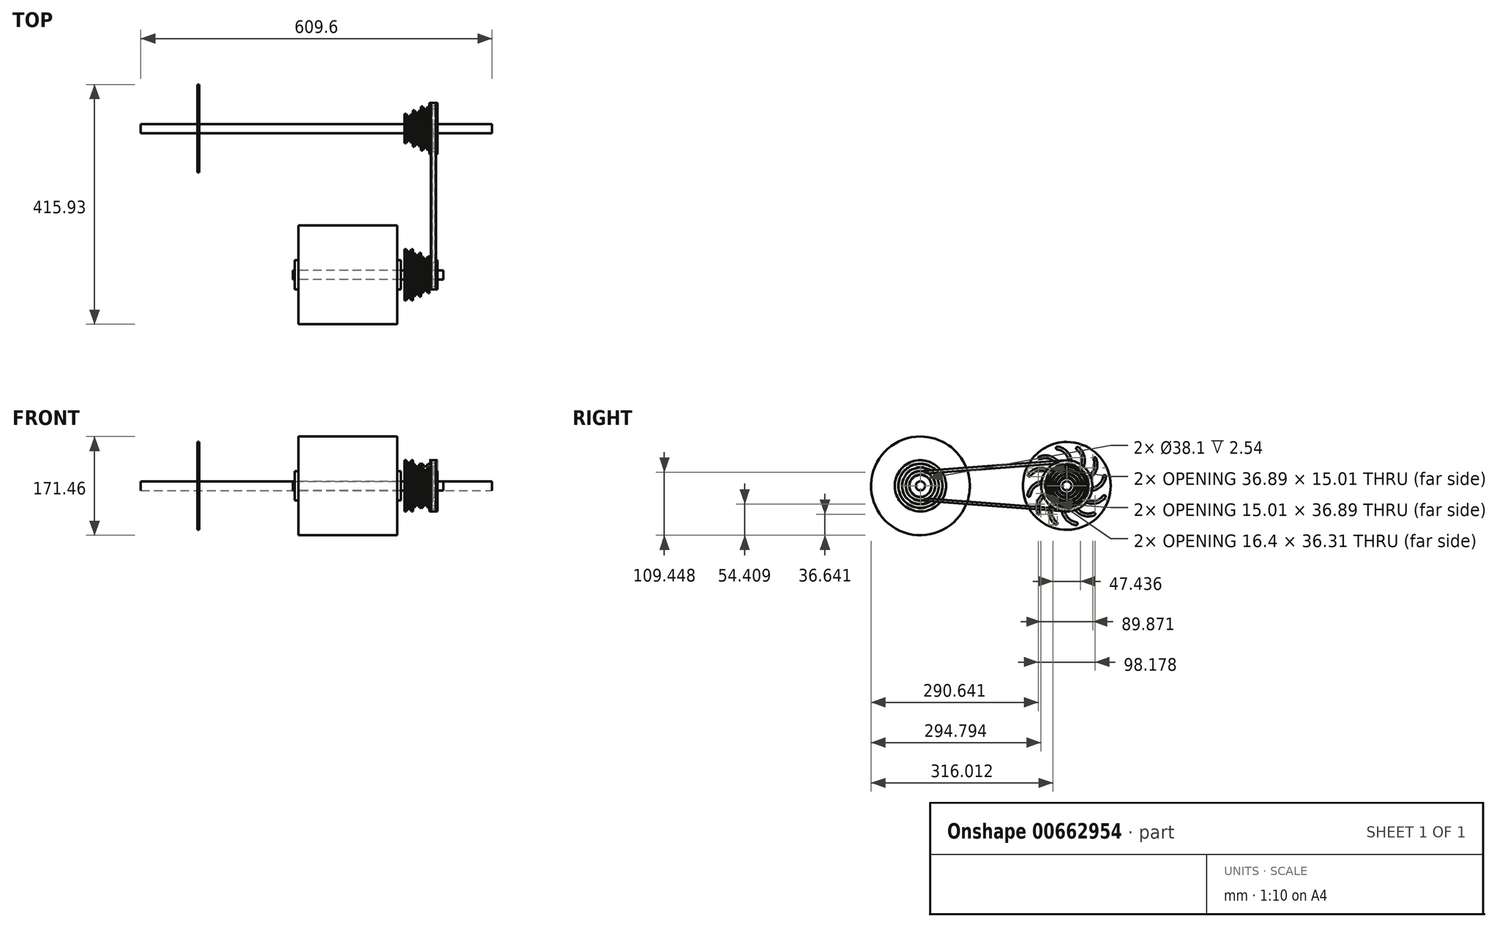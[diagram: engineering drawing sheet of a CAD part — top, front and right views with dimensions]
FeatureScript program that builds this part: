
annotation { "Feature Type Name" : "Feature", "Feature Type Description" : "" }
export const myFeature = defineFeature(function(context is Context, id is Id, definition is map)
    precondition{}
    {
        {
            var Q0;
            Q0=qCreatedBy(makeId("Right.planeOp"),FACE);
            var sketch = newSketch(context, id + "F0", { "sketchPlane" : qUnion([Q0])});
            skCircle(sketch, "E0", {"center": v(0, 0) * mm, "radius": 85.72 * mm});
            skCircle(sketch, "E1", {"center": v(0, 0) * mm, "radius": 25.4 * mm});
            skSolve(sketch);
        }
        {
            var Q0;
            Q0=qCreatedBy(makeId("Top.planeOp"),FACE);
            var sketch = newSketch(context, id + "F1", { "sketchPlane" : qUnion([Q0])});
            skLineSegment(sketch, "E2", {"start": v(65.11, 0) * mm, "end": v(190.35, 0) * mm, "construction": true});
            skLineSegment(sketch, "E3", {"start": v(-92.08, 0) * mm, "end": v(-92.08, 25.4) * mm});
            skLineSegment(sketch, "E4", {"start": v(-92.08, 25.4) * mm, "end": v(-85.73, 25.4) * mm});
            skLineSegment(sketch, "E5", {"start": v(-85.73, 25.4) * mm, "end": v(-85.73, 85.73) * mm});
            skLineSegment(sketch, "E6", {"start": v(0, 0) * mm, "end": v(0, 116.54) * mm, "construction": true});
            skLineSegment(sketch, "E7.MirrorCS", {"start": v(92.08, 25.4) * mm, "end": v(85.73, 25.4) * mm});
            skLineSegment(sketch, "E8.MirrorCS", {"start": v(92.08, 0) * mm, "end": v(92.08, 25.4) * mm});
            skLineSegment(sketch, "E9.MirrorCS", {"start": v(85.73, 25.4) * mm, "end": v(85.73, 85.73) * mm});
            skLineSegment(sketch, "E10", {"start": v(-85.72, 85.73) * mm, "end": v(85.72, 85.73) * mm});
            skLineSegment(sketch, "E11", {"start": v(-92.08, 0) * mm, "end": v(92.08, 0) * mm});
            skLineSegment(sketch, "E12.bottom", {"start": v(-95.25, 7.94) * mm, "end": v(165.4, 7.94) * mm});
            skLineSegment(sketch, "E12.top", {"start": v(-95.25, 0) * mm, "end": v(165.4, 0) * mm});
            skLineSegment(sketch, "E12.left", {"start": v(-95.25, 7.94) * mm, "end": v(-95.25, 0) * mm});
            skLineSegment(sketch, "E12.right", {"start": v(165.4, 7.94) * mm, "end": v(165.4, 0) * mm});
            skLineSegment(sketch, "E13", {"start": v(98.42, 44.45) * mm, "end": v(101.12, 44.45) * mm});
            skLineSegment(sketch, "E14", {"start": v(101.12, 44.45) * mm, "end": v(103.28, 39.88) * mm});
            skLineSegment(sketch, "E15", {"start": v(103.28, 39.88) * mm, "end": v(107.85, 39.88) * mm});
            skLineSegment(sketch, "E16", {"start": v(107.85, 39.88) * mm, "end": v(110.01, 44.45) * mm});
            skLineSegment(sketch, "E17", {"start": v(110.01, 44.45) * mm, "end": v(112.71, 44.45) * mm});
            skLineSegment(sketch, "E18", {"start": v(112.71, 44.45) * mm, "end": v(112.71, 38.1) * mm});
            skLineSegment(sketch, "E19.1.0.0", {"start": v(124.3, 38.1) * mm, "end": v(127, 38.1) * mm});
            skLineSegment(sketch, "E19.1.0.1", {"start": v(122.14, 33.53) * mm, "end": v(124.3, 38.1) * mm});
            skLineSegment(sketch, "E19.1.0.2", {"start": v(112.71, 38.1) * mm, "end": v(115.41, 38.1) * mm});
            skLineSegment(sketch, "E19.1.0.3", {"start": v(127, 38.1) * mm, "end": v(127, 31.75) * mm});
            skLineSegment(sketch, "E19.1.0.4", {"start": v(115.41, 38.1) * mm, "end": v(117.57, 33.53) * mm});
            skLineSegment(sketch, "E19.1.0.5", {"start": v(117.57, 33.53) * mm, "end": v(122.14, 33.53) * mm});
            skLineSegment(sketch, "E19.2.0.0", {"start": v(138.59, 31.75) * mm, "end": v(141.29, 31.75) * mm});
            skLineSegment(sketch, "E19.2.0.1", {"start": v(136.43, 27.18) * mm, "end": v(138.59, 31.75) * mm});
            skLineSegment(sketch, "E19.2.0.2", {"start": v(127, 31.75) * mm, "end": v(129.7, 31.75) * mm});
            skLineSegment(sketch, "E19.2.0.3", {"start": v(141.29, 31.75) * mm, "end": v(141.29, 25.4) * mm});
            skLineSegment(sketch, "E19.2.0.4", {"start": v(129.7, 31.75) * mm, "end": v(131.86, 27.18) * mm});
            skLineSegment(sketch, "E19.2.0.5", {"start": v(131.86, 27.18) * mm, "end": v(136.43, 27.18) * mm});
            skLineSegment(sketch, "E19.3.0.0", {"start": v(152.88, 25.4) * mm, "end": v(155.58, 25.4) * mm});
            skLineSegment(sketch, "E19.3.0.1", {"start": v(150.72, 20.83) * mm, "end": v(152.88, 25.4) * mm});
            skLineSegment(sketch, "E19.3.0.2", {"start": v(141.29, 25.4) * mm, "end": v(143.99, 25.4) * mm});
            skLineSegment(sketch, "E19.3.0.3", {"start": v(155.58, 25.4) * mm, "end": v(155.58, 19.05) * mm});
            skLineSegment(sketch, "E19.3.0.4", {"start": v(143.99, 25.4) * mm, "end": v(146.15, 20.83) * mm});
            skLineSegment(sketch, "E19.3.0.5", {"start": v(146.15, 20.83) * mm, "end": v(150.72, 20.83) * mm});
            skLineSegment(sketch, "E19.direction1", {"start": v(98.42, 44.45) * mm, "end": v(112.71, 38.1) * mm, "construction": true});
            skLineSegment(sketch, "E20", {"start": v(98.43, 44.45) * mm, "end": v(98.43, 7.94) * mm});
            skLineSegment(sketch, "E21", {"start": v(155.58, 19.05) * mm, "end": v(153.04, 19.05) * mm});
            skLineSegment(sketch, "E22", {"start": v(153.04, 19.05) * mm, "end": v(153.04, 7.94) * mm});
            skLineSegment(sketch, "E23", {"start": v(153.04, 7.94) * mm, "end": v(98.42, 7.94) * mm});
            skLineSegment(sketch, "E24.1.2", {"start": v(148.43, -49.75) * mm, "end": v(148.43, 40.41) * mm, "construction": true});
            skLineSegment(sketch, "E25.MirrorCS", {"start": v(150.72, -20.83) * mm, "end": v(152.88, -25.4) * mm});
            skLineSegment(sketch, "E26.MirrorCS", {"start": v(143.99, -25.4) * mm, "end": v(146.15, -20.83) * mm});
            skLineSegment(sketch, "E27.MirrorCS", {"start": v(146.15, -20.83) * mm, "end": v(150.72, -20.83) * mm});
            skLineSegment(sketch, "E28", {"start": v(143.99, -25.4) * mm, "end": v(152.88, -25.4) * mm});
            skLineSegment(sketch, "E29", {"start": v(127, 80.2) * mm, "end": v(127, 191.01) * mm, "construction": true});
            skLineSegment(sketch, "E30.1.0", {"start": v(107.85, 233.17) * mm, "end": v(103.28, 233.17) * mm});
            skLineSegment(sketch, "E30.1.1", {"start": v(117.57, 226.82) * mm, "end": v(115.41, 222.25) * mm});
            skLineSegment(sketch, "E30.1.2", {"start": v(152.88, 209.55) * mm, "end": v(150.72, 214.12) * mm});
            skLineSegment(sketch, "E30.1.3", {"start": v(127, 215.9) * mm, "end": v(127, 222.25) * mm});
            skLineSegment(sketch, "E30.1.4", {"start": v(124.3, 222.25) * mm, "end": v(122.14, 226.82) * mm});
            skLineSegment(sketch, "E30.1.5", {"start": v(98.42, 228.6) * mm, "end": v(98.42, 234.95) * mm});
            skLineSegment(sketch, "E30.1.6", {"start": v(100.96, 246.06) * mm, "end": v(155.58, 246.06) * mm});
            skLineSegment(sketch, "E30.1.7", {"start": v(101.12, 228.6) * mm, "end": v(98.42, 228.6) * mm});
            skLineSegment(sketch, "E30.1.8", {"start": v(112.71, 222.25) * mm, "end": v(112.71, 228.6) * mm});
            skLineSegment(sketch, "E30.1.9", {"start": v(103.28, 233.17) * mm, "end": v(101.12, 228.6) * mm});
            skLineSegment(sketch, "E30.1.10", {"start": v(122.14, 226.82) * mm, "end": v(117.57, 226.82) * mm});
            skLineSegment(sketch, "E30.1.11", {"start": v(100.96, 234.95) * mm, "end": v(100.96, 246.06) * mm});
            skLineSegment(sketch, "E30.1.12", {"start": v(146.15, 214.12) * mm, "end": v(143.99, 209.55) * mm});
            skLineSegment(sketch, "E30.1.13", {"start": v(155.58, 209.55) * mm, "end": v(141.29, 215.9) * mm, "construction": true});
            skLineSegment(sketch, "E30.1.14", {"start": v(155.58, 209.55) * mm, "end": v(155.58, 246.06) * mm});
            skLineSegment(sketch, "E30.1.15", {"start": v(110.01, 228.6) * mm, "end": v(107.85, 233.17) * mm});
            skLineSegment(sketch, "E30.1.16", {"start": v(141.29, 209.55) * mm, "end": v(141.29, 215.9) * mm});
            skLineSegment(sketch, "E30.1.17", {"start": v(131.86, 220.47) * mm, "end": v(129.7, 215.9) * mm});
            skLineSegment(sketch, "E30.1.18", {"start": v(150.72, 214.12) * mm, "end": v(146.15, 214.12) * mm});
            skLineSegment(sketch, "E30.1.19", {"start": v(136.43, 220.47) * mm, "end": v(131.86, 220.47) * mm});
            skLineSegment(sketch, "E30.1.20", {"start": v(138.59, 215.9) * mm, "end": v(136.43, 220.47) * mm});
            skLineSegment(sketch, "E30.1.21", {"start": v(115.41, 222.25) * mm, "end": v(112.71, 222.25) * mm});
            skLineSegment(sketch, "E30.1.22", {"start": v(155.58, 209.55) * mm, "end": v(152.88, 209.55) * mm});
            skLineSegment(sketch, "E30.1.23", {"start": v(112.71, 228.6) * mm, "end": v(110.01, 228.6) * mm});
            skLineSegment(sketch, "E30.1.24", {"start": v(143.99, 209.55) * mm, "end": v(141.29, 209.55) * mm});
            skLineSegment(sketch, "E30.1.25", {"start": v(98.43, 234.95) * mm, "end": v(100.96, 234.95) * mm});
            skLineSegment(sketch, "E30.1.26", {"start": v(127, 222.25) * mm, "end": v(124.3, 222.25) * mm});
            skLineSegment(sketch, "E30.1.27", {"start": v(141.29, 215.9) * mm, "end": v(138.59, 215.9) * mm});
            skLineSegment(sketch, "E30.1.28", {"start": v(129.7, 215.9) * mm, "end": v(127, 215.9) * mm});
            skLineSegment(sketch, "E30.1.29", {"start": v(188.89, 254) * mm, "end": v(63.65, 254) * mm, "construction": true});
            skPoint(sketch, "E30.center", {"position": v(127, 127) * mm});
            skSolve(sketch);
        }
        {
            var Q0;
            {var subQ1=sQuery(id+"F1.wireOp",EDGE,"E4");Q0=makeQuery(id+"F1.imprint","IMPRINT",FACE,{"disambiguationData":[TD([[makeQuery(id+"F1.imprint","IMPRINT",EDGE,{"derivedFrom":subQ1}),-1.0]])]});}
            var Q1;
            Q1=sQuery(id+"F1.wireOp",EDGE,"E2");
            revolve(context, id + "F2", {"entities" : qUnion([Q0]), "axis" : qUnion([Q1]), "revolveType" : RevolveType.FULL});
        }
        {
            var Q0;
            {var subQ5=sQuery(id+"F1.wireOp",EDGE,"E12.right");Q0=makeQuery(id+"F1.imprint","IMPRINT",FACE,{"disambiguationData":[TD([[makeQuery(id+"F1.imprint","IMPRINT",EDGE,{"derivedFrom":subQ5}),-1.0]])]});}
            var Q1;
            {var subQ0=sQuery(id+"F1.wireOp",EDGE,"E12.top");var subQ1=sQuery(id+"F1.wireOp",EDGE,"E3");var subQ2=makeQuery(id+"F1.imprint","INTERSECT",VERTEX,{"derivedFrom":[subQ1,subQ0]});Q1=makeQuery(id+"F1.imprint","IMPRINT",FACE,{"disambiguationData":[TD([[makeQuery(id+"F1.imprint","IMPRINT",EDGE,{"disambiguationData":[TD([[subQ2,-1.0]])],"derivedFrom":subQ1}),-1.0]])]});}
            var Q2;
            {var subQ5=sQuery(id+"F1.wireOp",EDGE,"E12.left");Q2=makeQuery(id+"F1.imprint","IMPRINT",FACE,{"disambiguationData":[TD([[makeQuery(id+"F1.imprint","IMPRINT",EDGE,{"derivedFrom":subQ5}),1.0]])]});}
            var Q3;
            Q3=sQuery(id+"F1.wireOp",EDGE,"E2");
            revolve(context, id + "F3", {"entities" : qUnion([Q0, Q1, Q2]), "axis" : qUnion([Q3]), "revolveType" : RevolveType.FULL});
        }
        {
            var Q0;
            Q0=makeQuery(id+"F1.imprint","IMPRINT",FACE,{"disambiguationData":[TD([[makeQuery(id+"F1.imprint","IMPRINT",EDGE,{"derivedFrom":sQuery(id+"F1.wireOp",EDGE,"E13")}),-1.0]])]});
            var Q1;
            Q1=sQuery(id+"F1.wireOp",EDGE,"E2");
            revolve(context, id + "F4", {"entities" : qUnion([Q0]), "axis" : qUnion([Q1]), "revolveType" : RevolveType.FULL});
        }
        {
            var Q0;
            Q0=makeQuery(id+"F1.imprint","IMPRINT",FACE,{"disambiguationData":[TD([[makeQuery(id+"F1.imprint","IMPRINT",EDGE,{"derivedFrom":sQuery(id+"F1.wireOp",EDGE,"E30.1.0")}),-1.0]])]});
            var Q1;
            Q1=sQuery(id+"F1.wireOp",EDGE,"E30.1.29");
            revolve(context, id + "F5", {"entities" : qUnion([Q0]), "axis" : qUnion([Q1]), "revolveType" : RevolveType.FULL});
        }
        {
            var Q0;
            Q0=qCreatedBy(makeId("Right.planeOp"),FACE);
            var Q1;
            Q1=sQuery(id+"F1.wireOp",VERTEX,"E24.1.2.start");
            cPlane(context, id + "F6", {"entities" : qUnion([Q0, Q1]), "cplaneType" : CPlaneType.PLANE_POINT, "offset" : 25.4 * mm, "width" : 152.4 * mm, "height" : 152.4 * mm});
        }
        {
            var Q0;
            Q0=qCreatedBy(id+"F6.planeOp",FACE);
            var sketch = newSketch(context, id + "F7", { "sketchPlane" : qUnion([Q0])});
            skLineSegment(sketch, "E31", {"start": v(250.67, 44.32) * mm, "end": v(-1.9, 25.33) * mm});
            skLineSegment(sketch, "E32", {"start": v(250.67, -44.32) * mm, "end": v(-1.9, -25.33) * mm});
            skArc(sketch, "E33", {"start": v(250.67, 44.32) * mm, "mid": v(298.45, 0) * mm, "end": v(250.67, -44.32) * mm});
            skArc(sketch, "E34", {"start": v(-1.9, 25.33) * mm, "mid": v(-25.4, 0) * mm, "end": v(-1.9, -25.33) * mm});
            skCircle(sketch, "E35", {"center": v(254, 0) * mm, "radius": 7.94 * mm});
            skSolve(sketch);
        }
        {
            var Q0;
            Q0=makeQuery(id+"F1.imprint","IMPRINT",FACE,{"disambiguationData":[TD([[makeQuery(id+"F1.imprint","IMPRINT",EDGE,{"derivedFrom":sQuery(id+"F1.wireOp",EDGE,"E25.MirrorCS")}),-1.0]])]});
            var Q1;
            Q1=sQuery(id+"F7.wireOp",EDGE,"E31");
            var Q2;
            Q2=sQuery(id+"F7.wireOp",EDGE,"E33");
            var Q3;
            Q3=sQuery(id+"F7.wireOp",EDGE,"E32");
            var Q4;
            Q4=sQuery(id+"F7.wireOp",EDGE,"E34");
            sweep(context, id + "F8", {"profiles" : qUnion([Q0]), "path" : qUnion([Q1, Q2, Q3, Q4])});
        }
        {
            var Q0;
            Q0=makeQuery(id+"F5.opRevolve","SWEPT_FACE",FACE,{"disambiguationData":[OSD([sQuery(id+"F1.wireOp",EDGE,"E30.1.14")])]});
            shell(context, id + "F9", {"entities" : qUnion([Q0]), "thickness" : 5.6 * mm});
        }
        {
            var Q0;
            Q0=makeQuery(id+"F7.imprint","IMPRINT",FACE,{"disambiguationData":[TD([[makeQuery(id+"F7.imprint","IMPRINT",EDGE,{"derivedFrom":sQuery(id+"F7.wireOp",EDGE,"E35")}),1.0]])]});
            extrude(context, id + "F10", {"entities" : qUnion([Q0]), "oppositeDirection" : true, "depth" : 508 * mm, "offsetDistance" : 25.4 * mm, "hasSecondDirection" : true, "secondDirectionOppositeDirection" : false, "secondDirectionDepth" : 101.6 * mm});
        }
        {
            var Q0;
            Q0=makeQuery(id+"F10.opExtrude","CAP_FACE",FACE,{"disambiguationData":[OSD([sQuery(id+"F7.wireOp",EDGE,"E35")])],"isStart":false});
            cPlane(context, id + "F11", {"entities" : qUnion([Q0]), "cplaneType" : CPlaneType.OFFSET, "offset" : 101.6 * mm, "oppositeDirection" : true, "width" : 152.4 * mm, "height" : 152.4 * mm});
        }
        {
            var Q0;
            Q0=qCreatedBy(id+"F11.planeOp",FACE);
            var sketch = newSketch(context, id + "F12", { "sketchPlane" : qUnion([Q0])});
            skCircle(sketch, "E36", {"center": v(-254, 0) * mm, "radius": 76.2 * mm});
            skArc(sketch, "E37", {"start": v(-295.8, -6.05) * mm, "mid": v(-311.68, 0.9) * mm, "end": v(-319.67, 16.28) * mm, "construction": true});
            skArc(sketch, "E38.0.startCap", {"start": v(-295.62, -3.52) * mm, "mid": v(-293.28, -6.24) * mm, "end": v(-296, -8.59) * mm});
            skArc(sketch, "E38.0.endCap", {"start": v(-322.18, 15.93) * mm, "mid": v(-320.02, 18.8) * mm, "end": v(-317.15, 16.64) * mm});
            skArc(sketch, "E38.0.left", {"start": v(-296, -8.59) * mm, "mid": v(-313.41, -0.95) * mm, "end": v(-322.18, 15.93) * mm});
            skArc(sketch, "E38.0.right", {"start": v(-295.62, -3.52) * mm, "mid": v(-309.94, 2.76) * mm, "end": v(-317.15, 16.64) * mm});
            skArc(sketch, "E39.1.0", {"start": v(-321.01, -20.3) * mm, "mid": v(-320.58, -16.73) * mm, "end": v(-317.01, -17.17) * mm});
            skArc(sketch, "E39.1.1", {"start": v(-286.08, -28.43) * mm, "mid": v(-304.98, -30.53) * mm, "end": v(-321.01, -20.3) * mm});
            skArc(sketch, "E39.1.2", {"start": v(-287.18, -26.15) * mm, "mid": v(-304.4, -28.05) * mm, "end": v(-319.01, -18.73) * mm, "construction": true});
            skArc(sketch, "E39.1.3", {"start": v(-288.28, -23.86) * mm, "mid": v(-284.9, -25.04) * mm, "end": v(-286.08, -28.43) * mm});
            skArc(sketch, "E39.1.4", {"start": v(-288.28, -23.86) * mm, "mid": v(-303.83, -25.58) * mm, "end": v(-317.01, -17.17) * mm});
            skArc(sketch, "E39.2.0", {"start": v(-301.89, -51.09) * mm, "mid": v(-303.3, -47.78) * mm, "end": v(-299.99, -46.38) * mm});
            skArc(sketch, "E39.2.1", {"start": v(-267.56, -40.66) * mm, "mid": v(-282.89, -51.93) * mm, "end": v(-301.89, -51.09) * mm});
            skArc(sketch, "E39.2.2", {"start": v(-269.66, -39.23) * mm, "mid": v(-283.62, -49.5) * mm, "end": v(-300.94, -48.73) * mm, "construction": true});
            skArc(sketch, "E39.2.3", {"start": v(-271.76, -37.8) * mm, "mid": v(-268.23, -37.13) * mm, "end": v(-267.56, -40.66) * mm});
            skArc(sketch, "E39.2.4", {"start": v(-271.76, -37.8) * mm, "mid": v(-284.36, -47.07) * mm, "end": v(-299.99, -46.38) * mm});
            skArc(sketch, "E39.3.0", {"start": v(-269.93, -68.18) * mm, "mid": v(-272.8, -66.02) * mm, "end": v(-270.64, -63.15) * mm});
            skArc(sketch, "E39.3.1", {"start": v(-245.41, -42) * mm, "mid": v(-253.05, -59.41) * mm, "end": v(-269.93, -68.18) * mm});
            skArc(sketch, "E39.3.2", {"start": v(-247.95, -41.8) * mm, "mid": v(-254.9, -57.68) * mm, "end": v(-270.28, -65.67) * mm, "construction": true});
            skArc(sketch, "E39.3.3", {"start": v(-250.48, -41.62) * mm, "mid": v(-247.76, -39.28) * mm, "end": v(-245.41, -42) * mm});
            skArc(sketch, "E39.3.4", {"start": v(-250.48, -41.62) * mm, "mid": v(-256.76, -55.94) * mm, "end": v(-270.64, -63.15) * mm});
            skArc(sketch, "E39.4.0", {"start": v(-233.7, -67.01) * mm, "mid": v(-237.27, -66.58) * mm, "end": v(-236.83, -63.01) * mm});
            skArc(sketch, "E39.4.1", {"start": v(-225.57, -32.08) * mm, "mid": v(-223.47, -50.98) * mm, "end": v(-233.7, -67.01) * mm});
            skArc(sketch, "E39.4.2", {"start": v(-227.85, -33.18) * mm, "mid": v(-225.95, -50.4) * mm, "end": v(-235.27, -65.01) * mm, "construction": true});
            skArc(sketch, "E39.4.3", {"start": v(-230.14, -34.28) * mm, "mid": v(-228.96, -30.9) * mm, "end": v(-225.57, -32.08) * mm});
            skArc(sketch, "E39.4.4", {"start": v(-230.14, -34.28) * mm, "mid": v(-228.42, -49.83) * mm, "end": v(-236.83, -63.01) * mm});
            skArc(sketch, "E39.5.0", {"start": v(-202.91, -47.89) * mm, "mid": v(-206.22, -49.3) * mm, "end": v(-207.62, -45.99) * mm});
            skArc(sketch, "E39.5.1", {"start": v(-213.34, -13.56) * mm, "mid": v(-202.07, -28.89) * mm, "end": v(-202.91, -47.89) * mm});
            skArc(sketch, "E39.5.2", {"start": v(-214.77, -15.66) * mm, "mid": v(-204.5, -29.62) * mm, "end": v(-205.27, -46.94) * mm, "construction": true});
            skArc(sketch, "E39.5.3", {"start": v(-216.2, -17.76) * mm, "mid": v(-216.87, -14.23) * mm, "end": v(-213.34, -13.56) * mm});
            skArc(sketch, "E39.5.4", {"start": v(-216.2, -17.76) * mm, "mid": v(-206.93, -30.36) * mm, "end": v(-207.62, -45.99) * mm});
            skArc(sketch, "E39.6.0", {"start": v(-185.82, -15.93) * mm, "mid": v(-187.98, -18.8) * mm, "end": v(-190.85, -16.64) * mm});
            skArc(sketch, "E39.6.1", {"start": v(-212, 8.59) * mm, "mid": v(-194.59, 0.95) * mm, "end": v(-185.82, -15.93) * mm});
            skArc(sketch, "E39.6.2", {"start": v(-212.2, 6.05) * mm, "mid": v(-196.32, -0.9) * mm, "end": v(-188.33, -16.28) * mm, "construction": true});
            skArc(sketch, "E39.6.3", {"start": v(-212.38, 3.52) * mm, "mid": v(-214.72, 6.24) * mm, "end": v(-212, 8.59) * mm});
            skArc(sketch, "E39.6.4", {"start": v(-212.38, 3.52) * mm, "mid": v(-198.06, -2.76) * mm, "end": v(-190.85, -16.64) * mm});
            skArc(sketch, "E39.7.0", {"start": v(-186.99, 20.3) * mm, "mid": v(-187.42, 16.73) * mm, "end": v(-190.99, 17.17) * mm});
            skArc(sketch, "E39.7.1", {"start": v(-221.92, 28.43) * mm, "mid": v(-203.02, 30.53) * mm, "end": v(-186.99, 20.3) * mm});
            skArc(sketch, "E39.7.2", {"start": v(-220.82, 26.15) * mm, "mid": v(-203.6, 28.05) * mm, "end": v(-188.99, 18.73) * mm, "construction": true});
            skArc(sketch, "E39.7.3", {"start": v(-219.72, 23.86) * mm, "mid": v(-223.1, 25.04) * mm, "end": v(-221.92, 28.43) * mm});
            skArc(sketch, "E39.7.4", {"start": v(-219.72, 23.86) * mm, "mid": v(-204.17, 25.58) * mm, "end": v(-190.99, 17.17) * mm});
            skArc(sketch, "E39.8.0", {"start": v(-206.11, 51.09) * mm, "mid": v(-204.7, 47.78) * mm, "end": v(-208.01, 46.38) * mm});
            skArc(sketch, "E39.8.1", {"start": v(-240.44, 40.66) * mm, "mid": v(-225.11, 51.93) * mm, "end": v(-206.11, 51.09) * mm});
            skArc(sketch, "E39.8.2", {"start": v(-238.34, 39.23) * mm, "mid": v(-224.38, 49.5) * mm, "end": v(-207.06, 48.73) * mm, "construction": true});
            skArc(sketch, "E39.8.3", {"start": v(-236.24, 37.8) * mm, "mid": v(-239.77, 37.13) * mm, "end": v(-240.44, 40.66) * mm});
            skArc(sketch, "E39.8.4", {"start": v(-236.24, 37.8) * mm, "mid": v(-223.64, 47.07) * mm, "end": v(-208.01, 46.38) * mm});
            skArc(sketch, "E39.9.0", {"start": v(-238.07, 68.18) * mm, "mid": v(-235.2, 66.02) * mm, "end": v(-237.36, 63.15) * mm});
            skArc(sketch, "E39.9.1", {"start": v(-262.59, 42) * mm, "mid": v(-254.95, 59.41) * mm, "end": v(-238.07, 68.18) * mm});
            skArc(sketch, "E39.9.2", {"start": v(-260.05, 41.8) * mm, "mid": v(-253.1, 57.68) * mm, "end": v(-237.72, 65.67) * mm, "construction": true});
            skArc(sketch, "E39.9.3", {"start": v(-257.52, 41.62) * mm, "mid": v(-260.24, 39.28) * mm, "end": v(-262.59, 42) * mm});
            skArc(sketch, "E39.9.4", {"start": v(-257.52, 41.62) * mm, "mid": v(-251.24, 55.94) * mm, "end": v(-237.36, 63.15) * mm});
            skArc(sketch, "E39.10.0", {"start": v(-274.3, 67.01) * mm, "mid": v(-270.73, 66.58) * mm, "end": v(-271.17, 63.01) * mm});
            skArc(sketch, "E39.10.1", {"start": v(-282.43, 32.08) * mm, "mid": v(-284.53, 50.98) * mm, "end": v(-274.3, 67.01) * mm});
            skArc(sketch, "E39.10.2", {"start": v(-280.15, 33.18) * mm, "mid": v(-282.05, 50.4) * mm, "end": v(-272.73, 65.01) * mm, "construction": true});
            skArc(sketch, "E39.10.3", {"start": v(-277.86, 34.28) * mm, "mid": v(-279.04, 30.9) * mm, "end": v(-282.43, 32.08) * mm});
            skArc(sketch, "E39.10.4", {"start": v(-277.86, 34.28) * mm, "mid": v(-279.58, 49.83) * mm, "end": v(-271.17, 63.01) * mm});
            skArc(sketch, "E39.11.0", {"start": v(-305.09, 47.89) * mm, "mid": v(-301.78, 49.3) * mm, "end": v(-300.38, 45.99) * mm});
            skArc(sketch, "E39.11.1", {"start": v(-294.66, 13.56) * mm, "mid": v(-305.93, 28.89) * mm, "end": v(-305.09, 47.89) * mm});
            skArc(sketch, "E39.11.2", {"start": v(-293.23, 15.66) * mm, "mid": v(-303.5, 29.62) * mm, "end": v(-302.73, 46.94) * mm, "construction": true});
            skArc(sketch, "E39.11.3", {"start": v(-291.8, 17.76) * mm, "mid": v(-291.13, 14.23) * mm, "end": v(-294.66, 13.56) * mm});
            skArc(sketch, "E39.11.4", {"start": v(-291.8, 17.76) * mm, "mid": v(-301.07, 30.36) * mm, "end": v(-300.38, 45.99) * mm});
            skSolve(sketch);
        }
        {
            var Q0;
            Q0=makeQuery(id+"F12.imprint","IMPRINT",FACE,{"disambiguationData":[TD([[makeQuery(id+"F12.imprint","IMPRINT",EDGE,{"derivedFrom":sQuery(id+"F12.wireOp",EDGE,"E36")}),1.0]])]});
            extrude(context, id + "F13", {"entities" : qUnion([Q0]), "depth" : 3.05 * mm, "offsetDistance" : 25.4 * mm});
        }
    });
